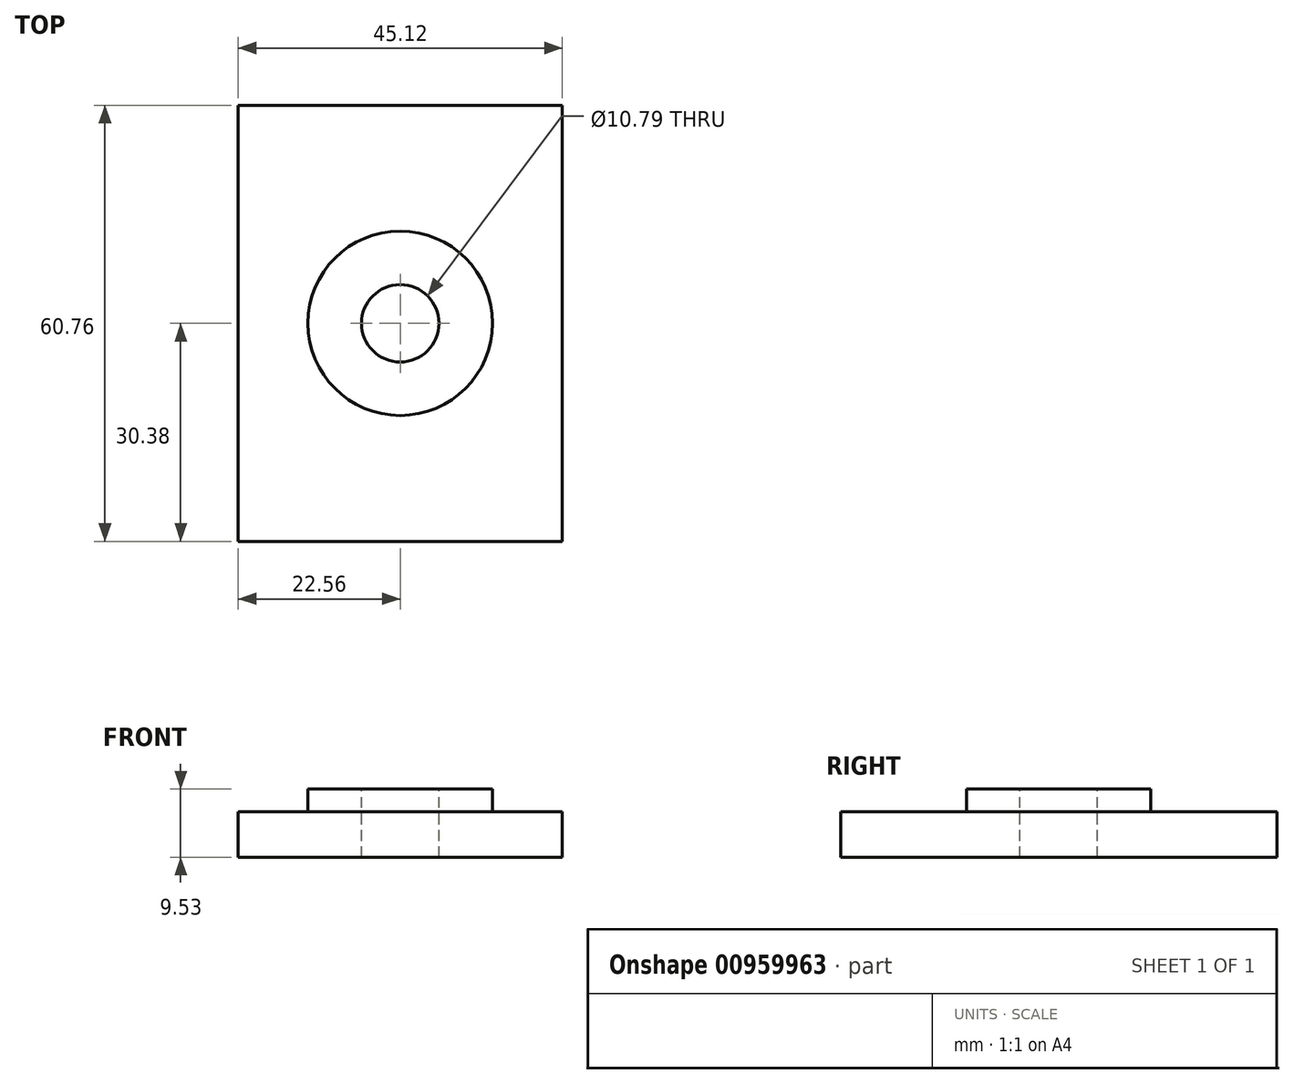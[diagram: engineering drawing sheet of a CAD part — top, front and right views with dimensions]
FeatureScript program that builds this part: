
annotation { "Feature Type Name" : "Feature", "Feature Type Description" : "" }
export const myFeature = defineFeature(function(context is Context, id is Id, definition is map)
    precondition{}
    {
        {
            var Q0;
            Q0=qCreatedBy(makeId("Top.planeOp"),FACE);
            var sketch = newSketch(context, id + "F0", { "sketchPlane" : qUnion([Q0])});
            skCircle(sketch, "E0", {"center": v(0, 0) * mm, "radius": 12.85 * mm});
            skCircle(sketch, "E1", {"center": v(0, 0) * mm, "radius": 5.4 * mm});
            skLineSegment(sketch, "E2.bottom", {"start": v(22.56, -30.38) * mm, "end": v(-22.56, -30.38) * mm});
            skLineSegment(sketch, "E2.top", {"start": v(22.56, 30.38) * mm, "end": v(-22.56, 30.38) * mm});
            skLineSegment(sketch, "E2.left", {"start": v(22.56, -30.38) * mm, "end": v(22.56, 30.38) * mm});
            skLineSegment(sketch, "E2.right", {"start": v(-22.56, -30.38) * mm, "end": v(-22.56, 30.38) * mm});
            skSolve(sketch);
        }
        {
            var Q0;
            Q0 = qSketchRegion(id + "F0", true);
            var Q1;
            Q1=makeQuery(id+"F0.imprint","IMPRINT",FACE,{"disambiguationData":[TD([[makeQuery(id+"F0.imprint","IMPRINT",EDGE,{"derivedFrom":sQuery(id+"F0.wireOp",EDGE,"E0")}),1.0]])]});
            extrude(context, id + "F1", {"entities" : qUnion([Q0, Q1]), "oppositeDirection" : true, "depth" : 6.35 * mm, "offsetDistance" : 25.4 * mm});
        }
        {
            var Q0;
            Q0=makeQuery(id+"F0.imprint","IMPRINT",FACE,{"disambiguationData":[TD([[makeQuery(id+"F0.imprint","IMPRINT",EDGE,{"derivedFrom":sQuery(id+"F0.wireOp",EDGE,"E0")}),1.0]])]});
            extrude(context, id + "F2", {"entities" : qUnion([Q0]), "operationType" : NewBodyOperationType.ADD, "depth" : 3.17 * mm, "offsetDistance" : 25.4 * mm});
        }
    });
